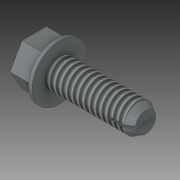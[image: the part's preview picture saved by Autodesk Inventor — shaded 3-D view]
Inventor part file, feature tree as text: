
AUTODESK INVENTOR PART (.ipt)
format: ipt  version: 2018 (Build 220112000, 112)  size: 125,440 bytes
history: native  units: in
note: dims shown in document units (in); Inventor stores cm internally (conversion verified against a paired STEP export)
features: other x4, thread x1
ambient origin geometry x8: Origin, YZ Plane, XZ Plane, XY Plane, X Axis, Y Axis, Z Axis, Center Point
bodies: Solid1 (feature_tree)
feature tree (5):
  other  "RIGHT"
  other  "TOP"
  other  "FRONT"
  thread  "Thread1"  [1 undecoded]
  other  "am-1310"
note: 1 required parameter value undecoded (feature->parameter linkage not recoverable at this tier; creation-order binding heuristic only, values carry confidence <= 0.55)
